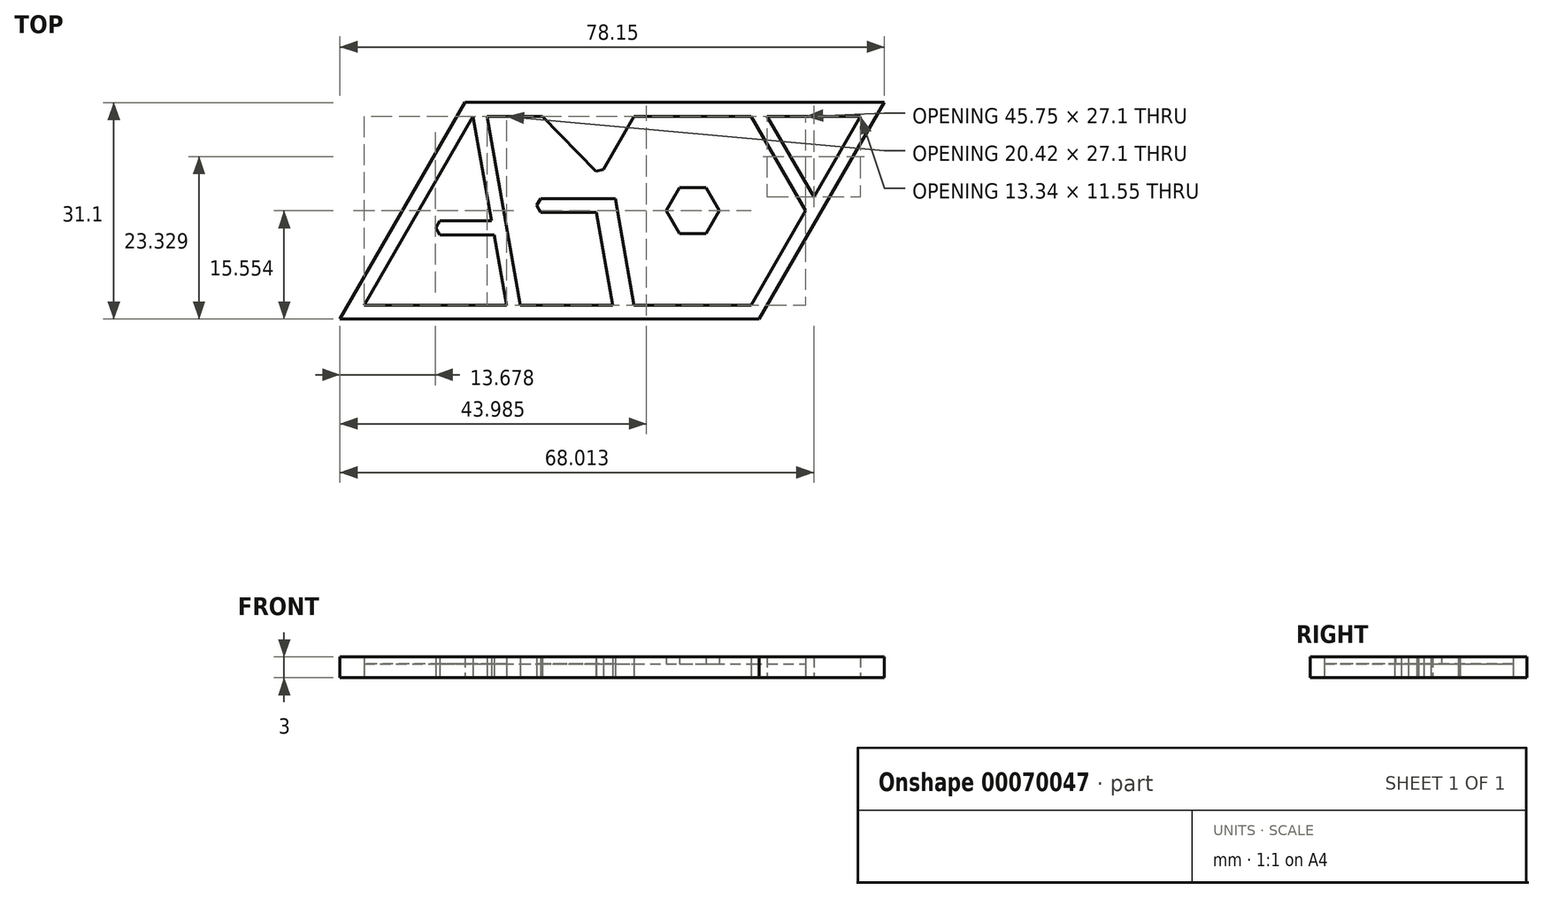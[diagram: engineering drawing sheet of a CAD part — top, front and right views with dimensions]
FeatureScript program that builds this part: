
annotation { "Feature Type Name" : "Feature", "Feature Type Description" : "" }
export const myFeature = defineFeature(function(context is Context, id is Id, definition is map)
    precondition{}
    {
        {
            var Q0;
            Q0=qCreatedBy(makeId("Top.planeOp"),FACE);
            var sketch = newSketch(context, id + "F0", { "sketchPlane" : qUnion([Q0])});
            skLineSegment(sketch, "E0", {"start": v(-58.85, -4.43) * mm, "end": v(-38.43, -4.43) * mm});
            skLineSegment(sketch, "E1", {"start": v(-38.43, -4.43) * mm, "end": v(-43.2, 22.67) * mm});
            skLineSegment(sketch, "E2", {"start": v(-43.2, 22.67) * mm, "end": v(-58.85, -4.43) * mm});
            skLineSegment(sketch, "E3", {"start": v(-40.2, 5.66) * mm, "end": v(-48, 5.66) * mm});
            skLineSegment(sketch, "E4", {"start": v(-38.43, -4.43) * mm, "end": v(-3.28, -4.43) * mm});
            skLineSegment(sketch, "E5", {"start": v(-43.2, 22.67) * mm, "end": v(-3.28, 22.67) * mm});
            skLineSegment(sketch, "E6", {"start": v(-3.28, -4.43) * mm, "end": v(4.54, 9.12) * mm});
            skLineSegment(sketch, "E7", {"start": v(4.54, 9.12) * mm, "end": v(-3.28, 22.67) * mm});
            skPoint(sketch, "E8.endSnap0", {"position": v(-40.82, 9.12) * mm});
            skLineSegment(sketch, "E9.0", {"start": v(-44.36, 24.67) * mm, "end": v(-2.86, 24.67) * mm});
            skLineSegment(sketch, "E9.1", {"start": v(-62.32, -6.43) * mm, "end": v(-38.92, -6.43) * mm});
            skLineSegment(sketch, "E9.2", {"start": v(-38.92, -6.43) * mm, "end": v(-2.13, -6.43) * mm});
            skLineSegment(sketch, "E9.3", {"start": v(-44.36, 24.67) * mm, "end": v(-62.32, -6.43) * mm});
            skLineSegment(sketch, "E9.4", {"start": v(-2.13, -6.43) * mm, "end": v(6.85, 9.12) * mm});
            skLineSegment(sketch, "E10", {"start": v(-48, 7.66) * mm, "end": v(-40.56, 7.66) * mm});
            skLineSegment(sketch, "E11", {"start": v(-41.2, 22.67) * mm, "end": v(-36.43, -4.43) * mm});
            skLineSegment(sketch, "E12", {"start": v(-43.2, 22.67) * mm, "end": v(-41.2, 22.67) * mm});
            skLineSegment(sketch, "E13", {"start": v(-23.52, -4.43) * mm, "end": v(-25.52, -4.43) * mm});
            skLineSegment(sketch, "E14", {"start": v(-33.49, 8.88) * mm, "end": v(-25.52, 8.88) * mm});
            skLineSegment(sketch, "E15", {"start": v(-22.8, 10.88) * mm, "end": v(-33.49, 10.88) * mm});
            skLineSegment(sketch, "E16", {"start": v(-25.6, 14.8) * mm, "end": v(-33.29, 22.67) * mm});
            skLineSegment(sketch, "E17", {"start": v(-48, 5.66) * mm, "end": v(-48.59, 6.66) * mm});
            skLineSegment(sketch, "E18", {"start": v(-48.59, 6.66) * mm, "end": v(-48, 7.66) * mm});
            skLineSegment(sketch, "E19", {"start": v(-33.49, 8.88) * mm, "end": v(-34.07, 9.88) * mm});
            skLineSegment(sketch, "E20", {"start": v(-34.07, 9.88) * mm, "end": v(-33.49, 10.88) * mm});
            skLineSegment(sketch, "E21", {"start": v(-24.17, 16.19) * mm, "end": v(-30.54, 22.67) * mm});
            skLineSegment(sketch, "E22", {"start": v(-25.6, 14.8) * mm, "end": v(-24.48, 15.08) * mm});
            skLineSegment(sketch, "E23", {"start": v(-24.48, 15.08) * mm, "end": v(-24.17, 16.19) * mm});
            skLineSegment(sketch, "E24", {"start": v(6.85, 9.12) * mm, "end": v(15.83, 24.67) * mm});
            skLineSegment(sketch, "E25", {"start": v(-2.86, 24.67) * mm, "end": v(15.83, 24.67) * mm});
            skLineSegment(sketch, "E26", {"start": v(5.7, 11.12) * mm, "end": v(12.36, 22.67) * mm});
            skLineSegment(sketch, "E27", {"start": v(5.7, 11.12) * mm, "end": v(-0.98, 22.67) * mm});
            skLineSegment(sketch, "E28", {"start": v(-0.98, 22.67) * mm, "end": v(12.36, 22.67) * mm});
            skLineSegment(sketch, "E29", {"start": v(-25.52, 8.88) * mm, "end": v(-23.18, -4.43) * mm});
            skLineSegment(sketch, "E30", {"start": v(-22.8, 10.88) * mm, "end": v(-20.1, -4.43) * mm});
            skLineSegment(sketch, "E31", {"start": v(-24.48, 15.08) * mm, "end": v(-20.1, 22.67) * mm});
            skLineSegment(sketch, "E32", {"start": v(-20.1, 22.67) * mm, "end": v(-3.28, 22.67) * mm});
            skLineSegment(sketch, "E33", {"start": v(-20.1, -4.43) * mm, "end": v(-3.28, -4.43) * mm});
            skPoint(sketch, "E34", {"position": v(-11.69, 22.67) * mm});
            skPoint(sketch, "E35", {"position": v(-11.69, 9.12) * mm});
            skCircle(sketch, "E36.cCircle", {"center": v(-11.69, 9.12) * mm, "radius": 3.3 * mm, "construction": true});
            skLineSegment(sketch, "E36.0", {"start": v(-13.6, 12.42) * mm, "end": v(-9.78, 12.42) * mm});
            skLineSegment(sketch, "E36.1", {"start": v(-9.78, 12.42) * mm, "end": v(-7.88, 9.12) * mm});
            skLineSegment(sketch, "E36.2", {"start": v(-7.88, 9.12) * mm, "end": v(-9.78, 5.82) * mm});
            skLineSegment(sketch, "E36.3", {"start": v(-9.78, 5.82) * mm, "end": v(-13.6, 5.82) * mm});
            skLineSegment(sketch, "E36.4", {"start": v(-13.6, 5.82) * mm, "end": v(-15.5, 9.12) * mm});
            skLineSegment(sketch, "E36.5", {"start": v(-15.5, 9.12) * mm, "end": v(-13.6, 12.42) * mm});
            skPoint(sketch, "E36.0.midPoint", {"position": v(-11.69, 12.42) * mm});
            skLineSegment(sketch, "E37", {"start": v(-62.32, -6.43) * mm, "end": v(-62.32, -16.43) * mm});
            skLineSegment(sketch, "E38", {"start": v(-62.32, -16.43) * mm, "end": v(-2.13, -16.43) * mm});
            skLineSegment(sketch, "E39", {"start": v(-2.13, -6.43) * mm, "end": v(-2.13, -16.43) * mm});
            skLineSegment(sketch, "E40", {"start": v(15.83, 24.67) * mm, "end": v(15.83, 14.67) * mm});
            skLineSegment(sketch, "E41", {"start": v(15.83, 14.67) * mm, "end": v(-2.13, -16.43) * mm});
            skSolve(sketch);
        }
        {
            var Q0;
            {var subQ3=sQuery(id+"F0.wireOp",EDGE,"E0");Q0=makeQuery(id+"F0.imprint","IMPRINT",FACE,{"disambiguationData":[TD([[makeQuery(id+"F0.imprint","IMPRINT",EDGE,{"derivedFrom":subQ3}),1.0]])]});}
            var Q1;
            {var subQ9=sQuery(id+"F0.wireOp",EDGE,"E6");Q1=makeQuery(id+"F0.imprint","IMPRINT",FACE,{"disambiguationData":[TD([[makeQuery(id+"F0.imprint","IMPRINT",EDGE,{"derivedFrom":subQ9}),1.0]])]});}
            extrude(context, id + "F1", {"entities" : qUnion([Q0, Q1]), "depth" : 2 * mm});
        }
        {
            var Q0;
            {var subQ3=sQuery(id+"F0.wireOp",EDGE,"E11");Q0=makeQuery(id+"F0.imprint","IMPRINT",FACE,{"disambiguationData":[TD([[makeQuery(id+"F0.imprint","IMPRINT",EDGE,{"derivedFrom":subQ3}),-1.0]])]});}
            var Q1;
            {var subQ0=sQuery(id+"F0.wireOp",EDGE,"E3");Q1=makeQuery(id+"F0.imprint","IMPRINT",FACE,{"disambiguationData":[TD([[makeQuery(id+"F0.imprint","IMPRINT",EDGE,{"derivedFrom":subQ0}),-1.0]])]});}
            var Q2;
            Q2=makeQuery(id+"F0.imprint","IMPRINT",FACE,{"disambiguationData":[TD([[makeQuery(id+"F0.imprint","IMPRINT",EDGE,{"derivedFrom":sQuery(id+"F0.wireOp",EDGE,"E14")}),1.0]])]});
            var Q3;
            Q3=makeQuery(id+"F0.imprint","IMPRINT",FACE,{"disambiguationData":[TD([[makeQuery(id+"F0.imprint","IMPRINT",EDGE,{"derivedFrom":sQuery(id+"F0.wireOp",EDGE,"2d3c4660-526b-4a69-8e3f-cc4842c2a15e")}),-1.0]])]});
            var Q4;
            {var subQ0=sQuery(id+"F0.wireOp",EDGE,"E16");Q4=makeQuery(id+"F0.imprint","IMPRINT",FACE,{"disambiguationData":[TD([[makeQuery(id+"F0.imprint","IMPRINT",EDGE,{"derivedFrom":subQ0}),-1.0]])]});}
            var Q5;
            {var subQ0=sQuery(id+"F0.wireOp",EDGE,"E21");Q5=makeQuery(id+"F0.imprint","IMPRINT",FACE,{"disambiguationData":[TD([[makeQuery(id+"F0.imprint","IMPRINT",EDGE,{"derivedFrom":subQ0}),-1.0]])]});}
            var Q6;
            {var subQ7=sQuery(id+"F0.wireOp",EDGE,"E0");Q6=makeQuery(id+"F0.imprint","IMPRINT",FACE,{"disambiguationData":[TD([[makeQuery(id+"F0.imprint","IMPRINT",EDGE,{"derivedFrom":subQ7}),-1.0]])]});}
            extrude(context, id + "F2", {"entities" : qUnion([Q0, Q1, Q2, Q3, Q4, Q5, Q6]), "depth" : 3 * mm});
        }
        {
            var Q0;
            Q0=makeQuery(id+"F0.imprint","IMPRINT",FACE,{"disambiguationData":[TD([[makeQuery(id+"F0.imprint","IMPRINT",EDGE,{"derivedFrom":sQuery(id+"F0.wireOp",EDGE,"E36.0")}),-1.0]])]});
            extrude(context, id + "F3", {"entities" : qUnion([Q0]), "operationType" : NewBodyOperationType.ADD, "depth" : 3 * mm});
        }
    });
